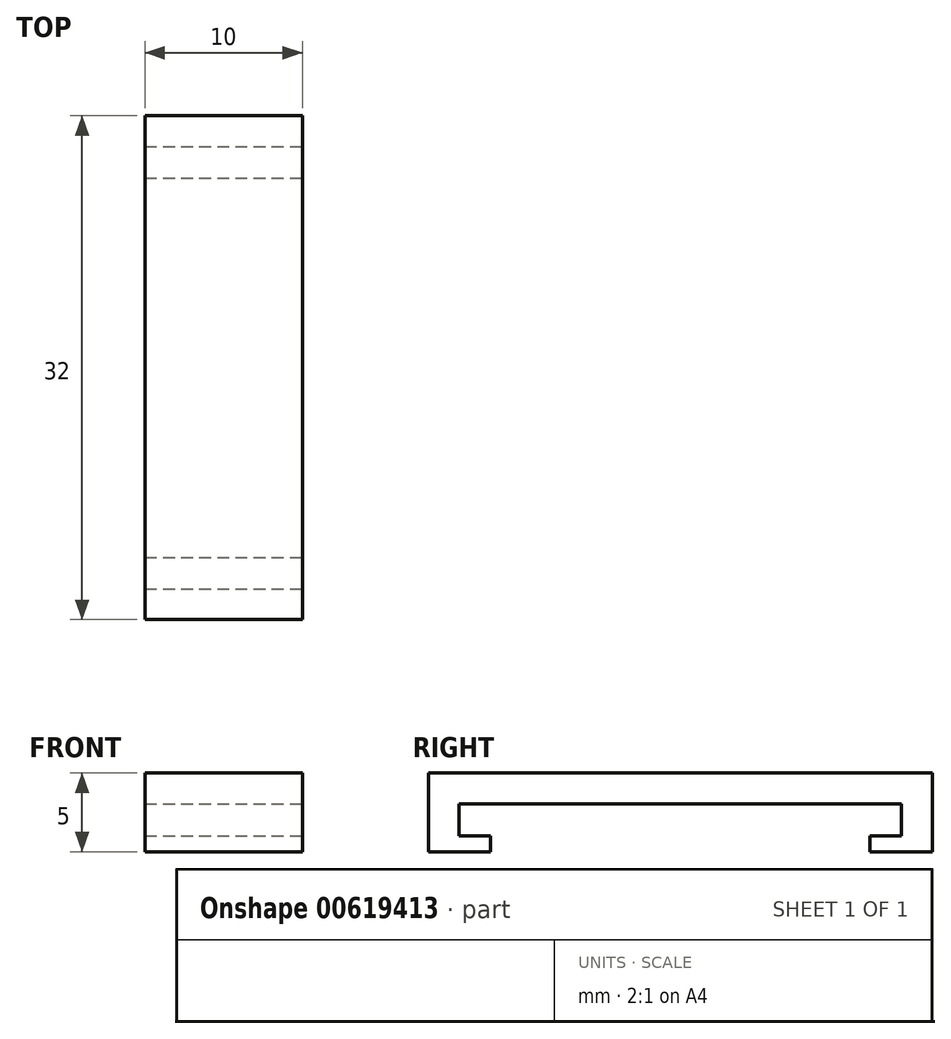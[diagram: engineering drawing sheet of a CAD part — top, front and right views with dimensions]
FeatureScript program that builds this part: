
annotation { "Feature Type Name" : "Feature", "Feature Type Description" : "" }
export const myFeature = defineFeature(function(context is Context, id is Id, definition is map)
    precondition{}
    {
        {
            var Q0;
            Q0=qCreatedBy(makeId("Top.planeOp"),FACE);
            var sketch = newSketch(context, id + "F0", { "sketchPlane" : qUnion([Q0])});
            skLineSegment(sketch, "E0.bottom", {"start": v(-5, 16) * mm, "end": v(5, 16) * mm});
            skLineSegment(sketch, "E0.top", {"start": v(-5, -16) * mm, "end": v(5, -16) * mm});
            skLineSegment(sketch, "E0.left", {"start": v(-5, 16) * mm, "end": v(-5, -16) * mm});
            skLineSegment(sketch, "E0.right", {"start": v(5, 16) * mm, "end": v(5, -16) * mm});
            skPoint(sketch, "E0.middle", {"position": v(0, 0) * mm});
            skSolve(sketch);
        }
        {
            var Q0;
            Q0=qSketchRegion(id+"F0",true);
            extrude(context, id + "F1", {"entities" : qUnion([Q0]), "depth" : 5 * mm, "offsetDistance" : 25 * mm});
        }
        {
            var Q0;
            Q0=makeQuery(id+"F1.opExtrude","SWEPT_FACE",FACE,{"disambiguationData":[OSD([sQuery(id+"F0.wireOp",EDGE,"E0.right")])]});
            var sketch = newSketch(context, id + "F2", { "sketchPlane" : qUnion([Q0])});
            skLineSegment(sketch, "E1", {"start": v(-12.05, 0) * mm, "end": v(-12.05, 1) * mm});
            skLineSegment(sketch, "E2", {"start": v(-12.05, 1) * mm, "end": v(-14.05, 1) * mm});
            skLineSegment(sketch, "E3", {"start": v(-14.05, 1) * mm, "end": v(-14.05, 3.05) * mm});
            skLineSegment(sketch, "E4", {"start": v(-14.05, 3.05) * mm, "end": v(14.05, 3.05) * mm});
            skLineSegment(sketch, "E5", {"start": v(14.05, 3.05) * mm, "end": v(14.05, 1) * mm});
            skLineSegment(sketch, "E6", {"start": v(14.05, 1) * mm, "end": v(12.05, 1) * mm});
            skLineSegment(sketch, "E7", {"start": v(12.05, 1) * mm, "end": v(12.05, 0) * mm});
            skSolve(sketch);
        }
        {
            var Q0;
            {var subQ0=sQuery(id+"F2.wireOp",EDGE,"E1");Q0=makeQuery(id+"F2.imprint","IMPRINT",FACE,{"disambiguationData":[TD([[makeQuery(id+"F2.imprint","IMPRINT",EDGE,{"derivedFrom":subQ0}),-1.0]])]});}
            extrude(context, id + "F3", {"entities" : qUnion([Q0]), "operationType" : NewBodyOperationType.REMOVE, "endBound" : BoundingType.THROUGH_ALL, "oppositeDirection" : true, "depth" : 25 * mm, "offsetDistance" : 25 * mm});
        }
    });
